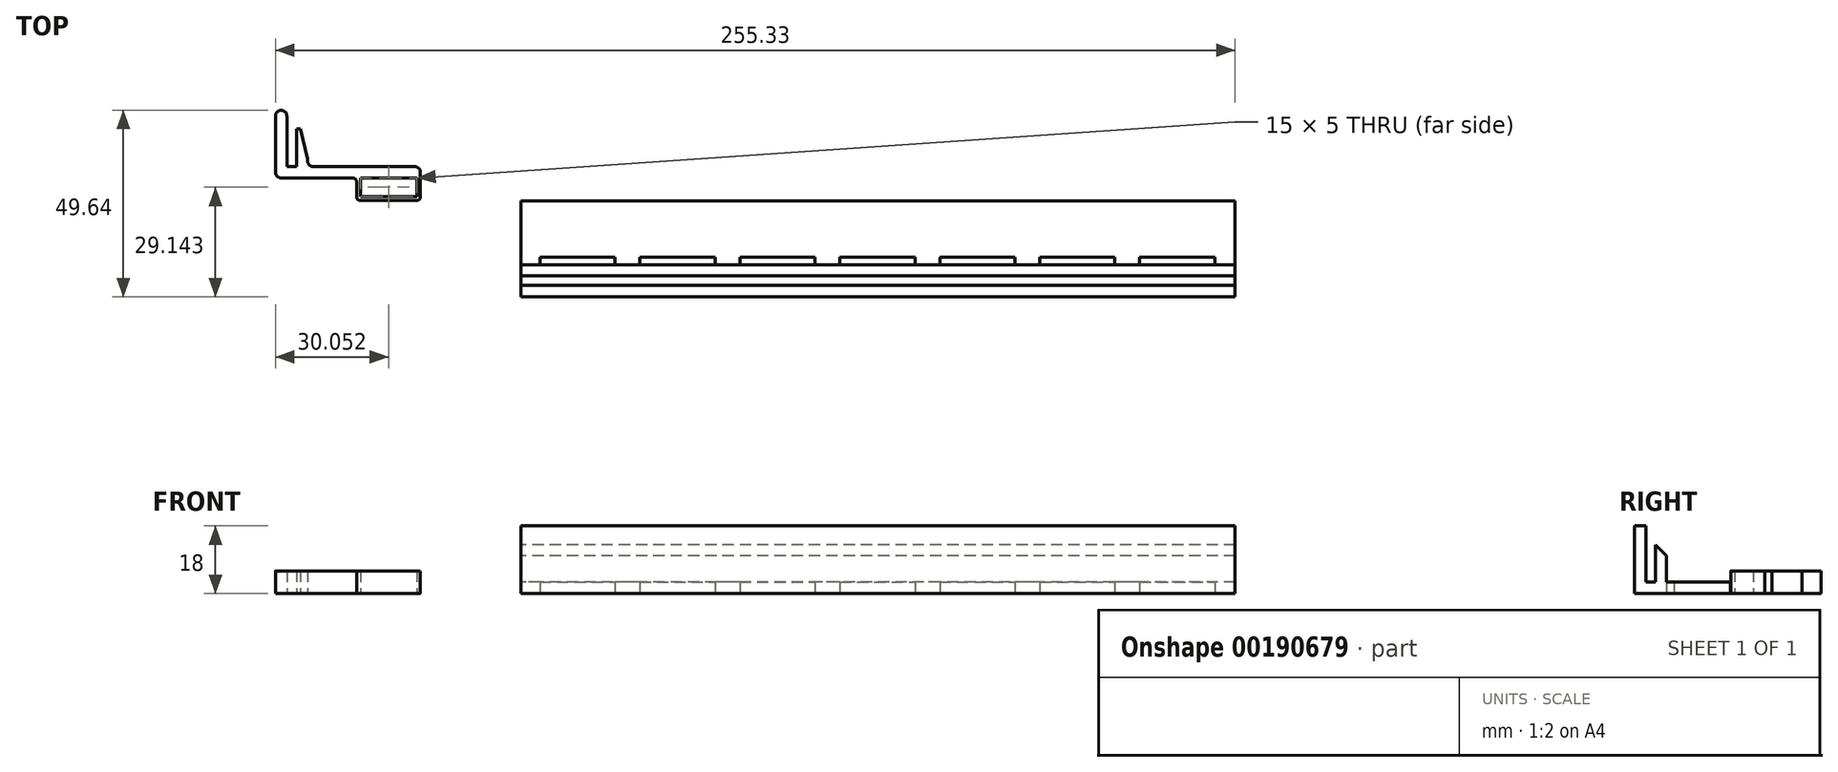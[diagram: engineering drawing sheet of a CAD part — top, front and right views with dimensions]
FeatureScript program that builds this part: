
annotation { "Feature Type Name" : "Feature", "Feature Type Description" : "" }
export const myFeature = defineFeature(function(context is Context, id is Id, definition is map)
    precondition{}
    {
        {
            var Q0;
            Q0=qCreatedBy(makeId("Right.planeOp"),FACE);
            var sketch = newSketch(context, id + "F0", { "sketchPlane" : qUnion([Q0])});
            skLineSegment(sketch, "E0", {"start": v(1.14, 13) * mm, "end": v(4.14, 10) * mm});
            skLineSegment(sketch, "E1", {"start": v(4.14, 10) * mm, "end": v(4.14, 3) * mm});
            skLineSegment(sketch, "E2", {"start": v(4.14, 3) * mm, "end": v(21.14, 3) * mm});
            skLineSegment(sketch, "E3", {"start": v(21.14, 3) * mm, "end": v(21.14, 0) * mm});
            skLineSegment(sketch, "E4", {"start": v(21.14, 0) * mm, "end": v(-2.42, 0) * mm});
            skLineSegment(sketch, "E5", {"start": v(1.14, 13) * mm, "end": v(1.14, 3) * mm});
            skLineSegment(sketch, "E6", {"start": v(1.14, 3) * mm, "end": v(-1.4, 3) * mm});
            skLineSegment(sketch, "E7", {"start": v(-1.4, 3) * mm, "end": v(-1.4, 18) * mm});
            skLineSegment(sketch, "E8", {"start": v(-1.4, 18) * mm, "end": v(-4.4, 18) * mm});
            skLineSegment(sketch, "E9", {"start": v(-4.4, 18) * mm, "end": v(-4.4, 0) * mm});
            skLineSegment(sketch, "E10", {"start": v(-4.4, 0) * mm, "end": v(-2.42, 0) * mm});
            skSolve(sketch);
        }
        {
            var Q0;
            Q0=makeQuery(id+"F0.imprint","IMPRINT",FACE,{"disambiguationData":[TD([[makeQuery(id+"F0.imprint","IMPRINT",EDGE,{"derivedFrom":sQuery(id+"F0.wireOp",EDGE,"E0")}),-1.0]])]});
            extrude(context, id + "F1", {"entities" : qUnion([Q0]), "depth" : 190 * mm});
        }
        {
            var Q0;
            Q0=makeQuery(id+"F1.opExtrude","SWEPT_FACE",FACE,{"disambiguationData":[OSD([sQuery(id+"F0.wireOp",EDGE,"E4"),sQuery(id+"F0.wireOp",EDGE,"E10")])]});
            var sketch = newSketch(context, id + "F2", { "sketchPlane" : qUnion([Q0])});
            skLineSegment(sketch, "E11.0", {"start": v(190, -4.14) * mm, "end": v(0, -4.14) * mm});
            skLineSegment(sketch, "E12.bottom", {"start": v(25, -6.14) * mm, "end": v(5, -6.14) * mm});
            skLineSegment(sketch, "E12.top", {"start": v(25, -4.14) * mm, "end": v(5, -4.14) * mm});
            skLineSegment(sketch, "E12.left", {"start": v(25, -6.14) * mm, "end": v(25, -4.14) * mm});
            skLineSegment(sketch, "E12.right", {"start": v(5, -6.14) * mm, "end": v(5, -4.14) * mm});
            skLineSegment(sketch, "E13.1.0.0", {"start": v(51.6, -6.14) * mm, "end": v(51.6, -4.14) * mm});
            skLineSegment(sketch, "E13.1.0.1", {"start": v(51.6, -4.14) * mm, "end": v(31.6, -4.14) * mm});
            skLineSegment(sketch, "E13.1.0.2", {"start": v(51.6, -6.14) * mm, "end": v(31.6, -6.14) * mm});
            skLineSegment(sketch, "E13.1.0.3", {"start": v(31.6, -6.14) * mm, "end": v(31.6, -4.14) * mm});
            skLineSegment(sketch, "E13.2.0.0", {"start": v(78.2, -6.14) * mm, "end": v(78.2, -4.14) * mm});
            skLineSegment(sketch, "E13.2.0.1", {"start": v(78.2, -4.14) * mm, "end": v(58.2, -4.14) * mm});
            skLineSegment(sketch, "E13.2.0.2", {"start": v(78.2, -6.14) * mm, "end": v(58.2, -6.14) * mm});
            skLineSegment(sketch, "E13.2.0.3", {"start": v(58.2, -6.14) * mm, "end": v(58.2, -4.14) * mm});
            skLineSegment(sketch, "E13.3.0.0", {"start": v(104.8, -6.14) * mm, "end": v(104.8, -4.14) * mm});
            skLineSegment(sketch, "E13.3.0.1", {"start": v(104.8, -4.14) * mm, "end": v(84.8, -4.14) * mm});
            skLineSegment(sketch, "E13.3.0.2", {"start": v(104.8, -6.14) * mm, "end": v(84.8, -6.14) * mm});
            skLineSegment(sketch, "E13.3.0.3", {"start": v(84.8, -6.14) * mm, "end": v(84.8, -4.14) * mm});
            skLineSegment(sketch, "E13.4.0.0", {"start": v(131.4, -6.14) * mm, "end": v(131.4, -4.14) * mm});
            skLineSegment(sketch, "E13.4.0.1", {"start": v(131.4, -4.14) * mm, "end": v(111.4, -4.14) * mm});
            skLineSegment(sketch, "E13.4.0.2", {"start": v(131.4, -6.14) * mm, "end": v(111.4, -6.14) * mm});
            skLineSegment(sketch, "E13.4.0.3", {"start": v(111.4, -6.14) * mm, "end": v(111.4, -4.14) * mm});
            skLineSegment(sketch, "E13.5.0.0", {"start": v(158, -6.14) * mm, "end": v(158, -4.14) * mm});
            skLineSegment(sketch, "E13.5.0.1", {"start": v(158, -4.14) * mm, "end": v(138, -4.14) * mm});
            skLineSegment(sketch, "E13.5.0.2", {"start": v(158, -6.14) * mm, "end": v(138, -6.14) * mm});
            skLineSegment(sketch, "E13.5.0.3", {"start": v(138, -6.14) * mm, "end": v(138, -4.14) * mm});
            skLineSegment(sketch, "E13.6.0.0", {"start": v(184.6, -6.14) * mm, "end": v(184.6, -4.14) * mm});
            skLineSegment(sketch, "E13.6.0.1", {"start": v(184.6, -4.14) * mm, "end": v(164.6, -4.14) * mm});
            skLineSegment(sketch, "E13.6.0.2", {"start": v(184.6, -6.14) * mm, "end": v(164.6, -6.14) * mm});
            skLineSegment(sketch, "E13.6.0.3", {"start": v(164.6, -6.14) * mm, "end": v(164.6, -4.14) * mm});
            skLineSegment(sketch, "E13.direction1", {"start": v(5, -6.14) * mm, "end": v(31.6, -6.14) * mm, "construction": true});
            skSolve(sketch);
        }
        {
            var Q0;
            Q0=makeQuery(id+"F2.imprint","IMPRINT",FACE,{"disambiguationData":[TD([[makeQuery(id+"F2.imprint","IMPRINT",EDGE,{"derivedFrom":sQuery(id+"F2.wireOp",EDGE,"E13.6.0.0")}),1.0]])]});
            var Q1;
            Q1=makeQuery(id+"F2.imprint","IMPRINT",FACE,{"disambiguationData":[TD([[makeQuery(id+"F2.imprint","IMPRINT",EDGE,{"derivedFrom":sQuery(id+"F2.wireOp",EDGE,"E13.5.0.0")}),1.0]])]});
            var Q2;
            Q2=makeQuery(id+"F2.imprint","IMPRINT",FACE,{"disambiguationData":[TD([[makeQuery(id+"F2.imprint","IMPRINT",EDGE,{"derivedFrom":sQuery(id+"F2.wireOp",EDGE,"E13.4.0.0")}),1.0]])]});
            var Q3;
            Q3=makeQuery(id+"F2.imprint","IMPRINT",FACE,{"disambiguationData":[TD([[makeQuery(id+"F2.imprint","IMPRINT",EDGE,{"derivedFrom":sQuery(id+"F2.wireOp",EDGE,"E13.3.0.0")}),1.0]])]});
            var Q4;
            Q4=makeQuery(id+"F2.imprint","IMPRINT",FACE,{"disambiguationData":[TD([[makeQuery(id+"F2.imprint","IMPRINT",EDGE,{"derivedFrom":sQuery(id+"F2.wireOp",EDGE,"E13.2.0.0")}),1.0]])]});
            var Q5;
            Q5=makeQuery(id+"F2.imprint","IMPRINT",FACE,{"disambiguationData":[TD([[makeQuery(id+"F2.imprint","IMPRINT",EDGE,{"derivedFrom":sQuery(id+"F2.wireOp",EDGE,"E13.1.0.0")}),1.0]])]});
            var Q6;
            Q6=makeQuery(id+"F2.imprint","IMPRINT",FACE,{"disambiguationData":[TD([[makeQuery(id+"F2.imprint","IMPRINT",EDGE,{"derivedFrom":sQuery(id+"F2.wireOp",EDGE,"E12.bottom")}),-1.0]])]});
            extrude(context, id + "F3", {"entities" : qUnion([Q0, Q1, Q2, Q3, Q4, Q5, Q6]), "operationType" : NewBodyOperationType.REMOVE, "oppositeDirection" : true, "depth" : 25 * mm});
        }
        {
            var Q0;
            Q0=qCreatedBy(makeId("Top.planeOp"),FACE);
            var sketch = newSketch(context, id + "F4", { "sketchPlane" : qUnion([Q0])});
            skLineSegment(sketch, "E14", {"start": v(-59.78, 40.23) * mm, "end": v(-56.78, 40.23) * mm});
            skLineSegment(sketch, "E15", {"start": v(-56.78, 40.23) * mm, "end": v(-56.78, 31.73) * mm});
            skLineSegment(sketch, "E16", {"start": v(-55.28, 30.23) * mm, "end": v(-28.28, 30.23) * mm});
            skLineSegment(sketch, "E17", {"start": v(-26.78, 28.73) * mm, "end": v(-26.78, 27.23) * mm});
            skLineSegment(sketch, "E18", {"start": v(-26.78, 27.23) * mm, "end": v(-50.34, 27.23) * mm});
            skLineSegment(sketch, "E19", {"start": v(-59.78, 40.23) * mm, "end": v(-59.78, 30.23) * mm});
            skLineSegment(sketch, "E20", {"start": v(-59.78, 30.23) * mm, "end": v(-62.33, 30.23) * mm});
            skLineSegment(sketch, "E21", {"start": v(-62.33, 30.23) * mm, "end": v(-62.33, 43.73) * mm});
            skLineSegment(sketch, "E22", {"start": v(-63.83, 45.23) * mm, "end": v(-63.83, 45.23) * mm});
            skLineSegment(sketch, "E23", {"start": v(-65.33, 43.73) * mm, "end": v(-65.33, 28.73) * mm});
            skLineSegment(sketch, "E24", {"start": v(-63.83, 27.23) * mm, "end": v(-50.34, 27.23) * mm});
            skPoint(sketch, "E25.visualSharp", {"position": v(-62.33, 45.23) * mm});
            skArc(sketch, "E25.filletArc", {"start": v(-62.33, 43.73) * mm, "mid": v(-62.77, 44.8) * mm, "end": v(-63.83, 45.23) * mm});
            skPoint(sketch, "E26.visualSharp", {"position": v(-65.33, 45.23) * mm});
            skArc(sketch, "E26.filletArc", {"start": v(-63.83, 45.23) * mm, "mid": v(-64.89, 44.8) * mm, "end": v(-65.33, 43.73) * mm});
            skPoint(sketch, "E27.visualSharp", {"position": v(-26.78, 30.23) * mm});
            skArc(sketch, "E27.filletArc", {"start": v(-26.78, 28.73) * mm, "mid": v(-27.22, 29.8) * mm, "end": v(-28.28, 30.23) * mm});
            skPoint(sketch, "E28.visualSharp", {"position": v(-65.33, 27.23) * mm});
            skArc(sketch, "E28.filletArc", {"start": v(-65.33, 28.73) * mm, "mid": v(-64.89, 27.67) * mm, "end": v(-63.83, 27.23) * mm});
            skPoint(sketch, "E29.visualSharp", {"position": v(-56.78, 30.23) * mm});
            skArc(sketch, "E29.filletArc", {"start": v(-56.78, 31.73) * mm, "mid": v(-56.34, 30.67) * mm, "end": v(-55.28, 30.23) * mm});
            skLineSegment(sketch, "E30.bottom", {"start": v(-26.78, 27.23) * mm, "end": v(-43.78, 27.23) * mm});
            skLineSegment(sketch, "E30.top", {"start": v(-26.78, 21.23) * mm, "end": v(-43.78, 21.23) * mm});
            skLineSegment(sketch, "E30.left", {"start": v(-26.78, 27.23) * mm, "end": v(-26.78, 21.23) * mm});
            skLineSegment(sketch, "E30.right", {"start": v(-43.78, 27.23) * mm, "end": v(-43.78, 21.23) * mm});
            skLineSegment(sketch, "E31.bottom", {"start": v(-42.78, 27.23) * mm, "end": v(-27.78, 27.23) * mm});
            skLineSegment(sketch, "E31.top", {"start": v(-42.78, 22.23) * mm, "end": v(-27.78, 22.23) * mm});
            skLineSegment(sketch, "E31.left", {"start": v(-42.78, 27.23) * mm, "end": v(-42.78, 22.23) * mm});
            skLineSegment(sketch, "E31.right", {"start": v(-27.78, 27.23) * mm, "end": v(-27.78, 22.23) * mm});
            skSolve(sketch);
        }
        {
            var Q0;
            Q0=makeQuery(id+"F4.imprint","IMPRINT",FACE,{"disambiguationData":[TD([[makeQuery(id+"F4.imprint","IMPRINT",EDGE,{"derivedFrom":sQuery(id+"F4.wireOp",EDGE,"E14")}),-1.0]])]});
            var Q1;
            Q1=makeQuery(id+"F4.imprint","IMPRINT",FACE,{"disambiguationData":[TD([[makeQuery(id+"F4.imprint","IMPRINT",EDGE,{"derivedFrom":sQuery(id+"F4.wireOp",EDGE,"E30.top")}),-1.0]])]});
            extrude(context, id + "F5", {"entities" : qUnion([Q0, Q1]), "depth" : 6 * mm});
        }
        {
            var Q0;
            Q0=makeQuery(id+"F5.opExtrude","SWEPT_EDGE",EDGE,{"disambiguationData":[OSD([sQuery(id+"F4.wireOp",EDGE,"E14"),sQuery(id+"F4.wireOp",EDGE,"E15")])]});
            chamfer(context, id + "F6", {"entities" : qUnion([Q0]), "chamferType" : ChamferType.TWO_OFFSETS, "width1" : 2 * mm, "oppositeDirection" : false, "width2" : 8 * mm, "tangentPropagation" : true});
        }
        {
            var Q0;
            Q0=makeQuery(id+"F5.opExtrude","SWEPT_EDGE",EDGE,{"disambiguationData":[OSD([sQuery(id+"F4.wireOp",EDGE,"E18"),sQuery(id+"F4.wireOp",EDGE,"E30.right")])]});
            var Q1;
            Q1=makeQuery(id+"F5.opExtrude","SWEPT_EDGE",EDGE,{"disambiguationData":[OSD([sQuery(id+"F4.wireOp",EDGE,"E30.top"),sQuery(id+"F4.wireOp",EDGE,"E30.right")])]});
            var Q2;
            Q2=makeQuery(id+"F5.opExtrude","SWEPT_EDGE",EDGE,{"disambiguationData":[OSD([sQuery(id+"F4.wireOp",EDGE,"E30.top"),sQuery(id+"F4.wireOp",EDGE,"E30.left")])]});
            fillet(context, id + "F7", {"entities" : qUnion([Q0, Q1, Q2]), "radius" : 1 * mm, "tangentPropagation" : true, "allowEdgeOverflow" : false});
        }
    });
